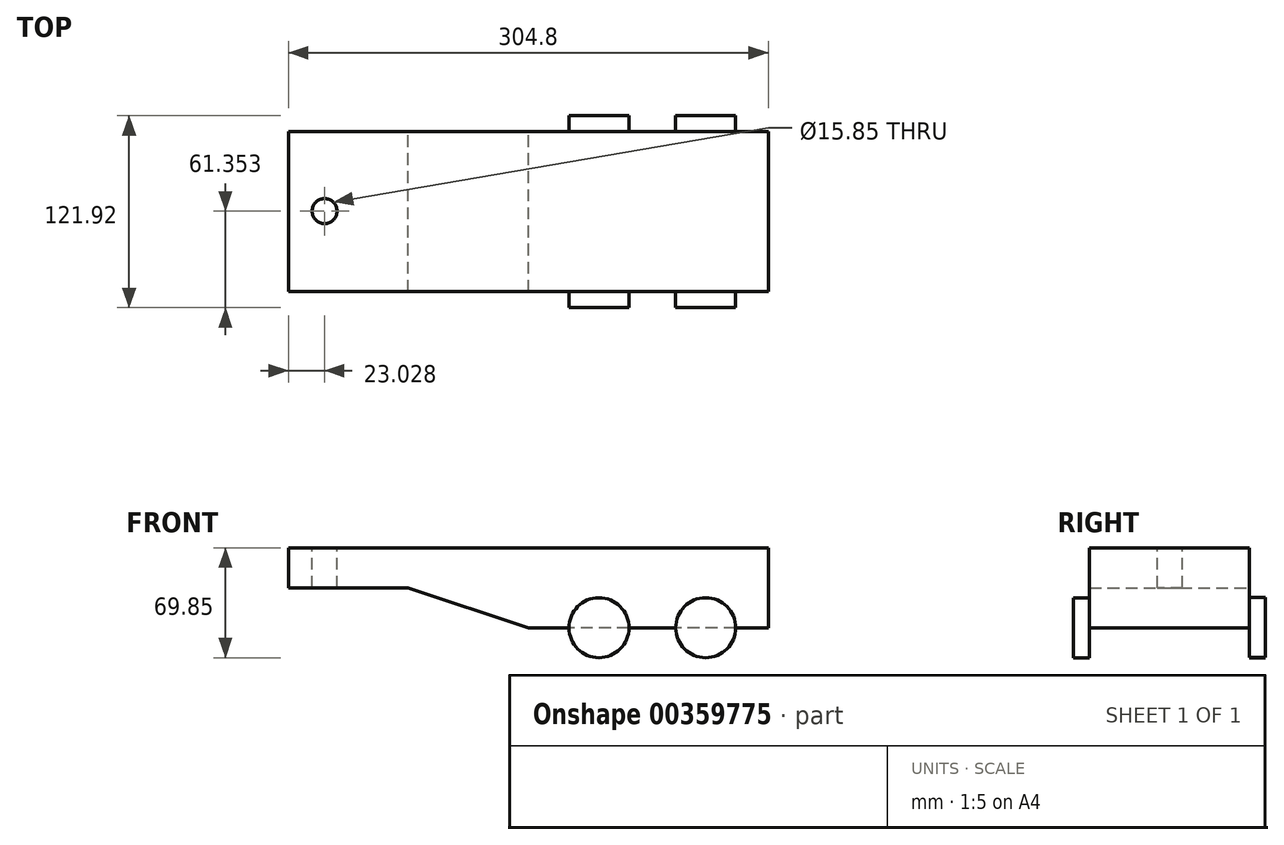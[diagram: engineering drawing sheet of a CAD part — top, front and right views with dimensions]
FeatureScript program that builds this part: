
annotation { "Feature Type Name" : "Feature", "Feature Type Description" : "" }
export const myFeature = defineFeature(function(context is Context, id is Id, definition is map)
    precondition{}
    {
        {
            var Q0;
            Q0=qCreatedBy(makeId("Front.planeOp"),FACE);
            var sketch = newSketch(context, id + "F0", { "sketchPlane" : qUnion([Q0])});
            skLineSegment(sketch, "E0.bottom", {"start": v(152.4, -25.4) * mm, "end": v(-152.4, -25.4) * mm});
            skLineSegment(sketch, "E0.top", {"start": v(152.4, 25.4) * mm, "end": v(-152.4, 25.4) * mm});
            skLineSegment(sketch, "E0.left", {"start": v(152.4, -25.4) * mm, "end": v(152.4, 25.4) * mm});
            skLineSegment(sketch, "E0.right", {"start": v(-152.4, -25.4) * mm, "end": v(-152.4, 25.4) * mm});
            skPoint(sketch, "E0.middle", {"position": v(0, 0) * mm});
            skLineSegment(sketch, "E1", {"start": v(-152.4, 0) * mm, "end": v(-76.2, 0) * mm});
            skLineSegment(sketch, "E2", {"start": v(-76.2, 0) * mm, "end": v(0, -25.4) * mm});
            skSolve(sketch);
        }
        {
            var Q0;
            {var subQ1=sQuery(id+"F0.wireOp",EDGE,"E0.top");Q0=makeQuery(id+"F0.imprint","IMPRINT",FACE,{"disambiguationData":[TD([[makeQuery(id+"F0.imprint","IMPRINT",EDGE,{"derivedFrom":subQ1}),1.0]])]});}
            extrude(context, id + "F1", {"entities" : qUnion([Q0]), "depth" : 101.6 * mm});
        }
        {
            var Q0;
            Q0=qCreatedBy(makeId("Front.planeOp"),FACE);
            var sketch = newSketch(context, id + "F2", { "sketchPlane" : qUnion([Q0])});
            skCircle(sketch, "E3", {"center": v(44.88, -25.34) * mm, "radius": 19.05 * mm});
            skCircle(sketch, "E4", {"center": v(112.67, -25.2) * mm, "radius": 19.05 * mm});
            skSolve(sketch);
        }
        {
            var Q0;
            Q0=makeQuery(id+"F1.opExtrude","CAP_FACE",FACE,{"disambiguationData":[OSD([sQuery(id+"F0.wireOp",EDGE,"E0.bottom"),sQuery(id+"F0.wireOp",EDGE,"E0.top"),sQuery(id+"F0.wireOp",EDGE,"E0.left"),sQuery(id+"F0.wireOp",EDGE,"E0.right"),sQuery(id+"F0.wireOp",EDGE,"E1"),sQuery(id+"F0.wireOp",EDGE,"E2")])],"isStart":false});
            var sketch = newSketch(context, id + "F3", { "sketchPlane" : qUnion([Q0])});
            skCircle(sketch, "E5", {"center": v(44.88, -25.4) * mm, "radius": 19.05 * mm});
            skCircle(sketch, "E6", {"center": v(112.66, -25.4) * mm, "radius": 19.05 * mm});
            skSolve(sketch);
        }
        {
            var Q0;
            Q0 = qSketchRegion(id + "F3", true);
            extrude(context, id + "F4", {"entities" : qUnion([Q0]), "operationType" : NewBodyOperationType.ADD, "depth" : 10.16 * mm});
        }
        {
            var Q0;
            Q0=makeQuery(id+"F1.opExtrude","SWEPT_FACE",FACE,{"disambiguationData":[OSD([sQuery(id+"F0.wireOp",EDGE,"E0.top")])]});
            var sketch = newSketch(context, id + "F5", { "sketchPlane" : qUnion([Q0])});
            skLineSegment(sketch, "E7", {"start": v(-152.4, -50.8) * mm, "end": v(-137.29, -50.8) * mm});
            skCircle(sketch, "E8", {"center": v(-129.37, -50.4) * mm, "radius": 7.92 * mm});
            skPoint(sketch, "E8.second.point", {"position": v(-121.46, -50.8) * mm});
            skPoint(sketch, "E8.third.point", {"position": v(-126.54, -57.8) * mm});
            skSolve(sketch);
        }
        {
            var Q0;
            Q0 = qSketchRegion(id + "F5", true);
            extrude(context, id + "F6", {"entities" : qUnion([Q0]), "operationType" : NewBodyOperationType.ADD, "depth" : 25.4 * mm});
        }
        {
            var Q0;
            Q0=makeQuery(id+"F6.opExtrude","CAP_FACE",FACE,{"disambiguationData":[OSD([sQuery(id+"F5.wireOp",EDGE,"E8")])],"isStart":false});
            extrude(context, id + "F7", {"entities" : qUnion([Q0]), "operationType" : NewBodyOperationType.REMOVE, "endBound" : BoundingType.THROUGH_ALL, "oppositeDirection" : true, "depth" : 25.4 * mm});
        }
        {
            var Q0;
            Q0=makeQuery(id+"F2.imprint","IMPRINT",FACE,{"disambiguationData":[TD([[makeQuery(id+"F2.imprint","IMPRINT",EDGE,{"derivedFrom":sQuery(id+"F2.wireOp",EDGE,"E4")}),1.0]])]});
            var Q1;
            Q1=makeQuery(id+"F2.imprint","IMPRINT",FACE,{"disambiguationData":[TD([[makeQuery(id+"F2.imprint","IMPRINT",EDGE,{"derivedFrom":sQuery(id+"F2.wireOp",EDGE,"E3")}),1.0]])]});
            extrude(context, id + "F8", {"entities" : qUnion([Q0, Q1]), "operationType" : NewBodyOperationType.ADD, "oppositeDirection" : true, "depth" : 10.16 * mm});
        }
    });
